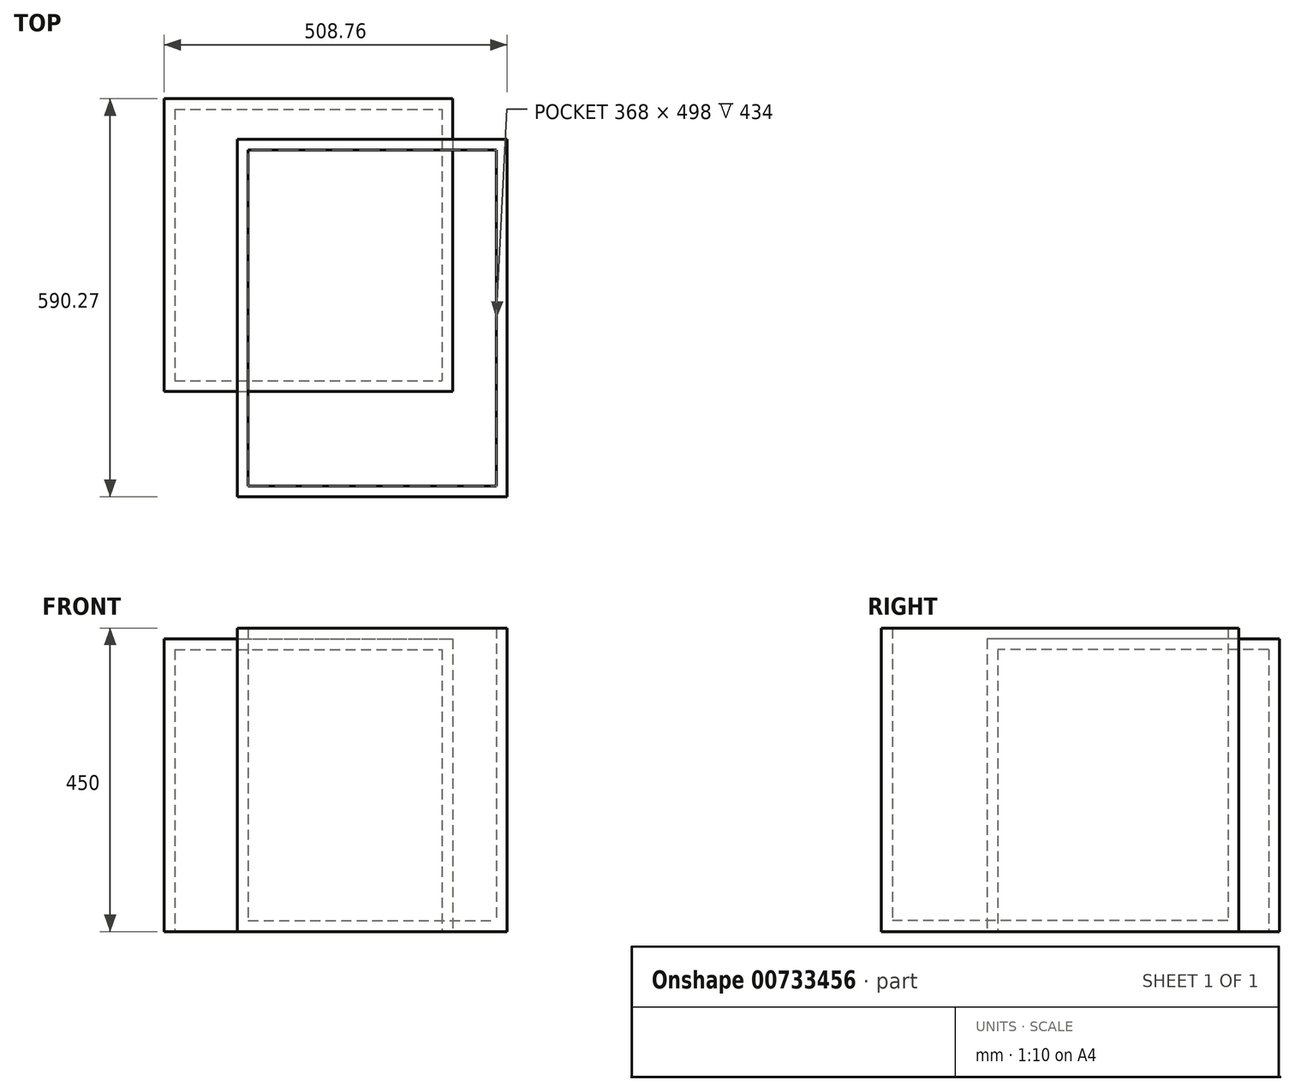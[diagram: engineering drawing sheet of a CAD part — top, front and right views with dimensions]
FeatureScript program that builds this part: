
annotation { "Feature Type Name" : "Feature", "Feature Type Description" : "" }
export const myFeature = defineFeature(function(context is Context, id is Id, definition is map)
    precondition{}
    {
        {
            var Q0;
            Q0=qCreatedBy(makeId("Top.planeOp"),FACE);
            var sketch = newSketch(context, id + "F0", { "sketchPlane" : qUnion([Q0])});
            skLineSegment(sketch, "E0.bottom", {"start": v(-203.64, 308.13) * mm, "end": v(196.36, 308.13) * mm});
            skLineSegment(sketch, "E0.top", {"start": v(-203.64, -221.87) * mm, "end": v(196.36, -221.87) * mm});
            skLineSegment(sketch, "E0.left", {"start": v(-203.64, 308.13) * mm, "end": v(-203.64, -221.87) * mm});
            skLineSegment(sketch, "E0.right", {"start": v(196.36, 308.13) * mm, "end": v(196.36, -221.87) * mm});
            skSolve(sketch);
        }
        {
            var Q0;
            Q0=makeQuery(id+"F0.imprint","IMPRINT",FACE,{"disambiguationData":[TD([[makeQuery(id+"F0.imprint","IMPRINT",EDGE,{"derivedFrom":sQuery(id+"F0.wireOp",EDGE,"E0.bottom")}),-1.0]])]});
            var sketch = newSketch(context, id + "F1", { "sketchPlane" : qUnion([Q0])});
            skLineSegment(sketch, "E1.bottom", {"start": v(-312.4, 368.4) * mm, "end": v(115.6, 368.4) * mm});
            skLineSegment(sketch, "E1.top", {"start": v(-312.4, -65.6) * mm, "end": v(115.6, -65.6) * mm});
            skLineSegment(sketch, "E1.left", {"start": v(-312.4, 368.4) * mm, "end": v(-312.4, -65.6) * mm});
            skLineSegment(sketch, "E1.right", {"start": v(115.6, 368.4) * mm, "end": v(115.6, -65.6) * mm});
            skSolve(sketch);
        }
        {
            var Q0;
            Q0 = qSketchRegion(id + "F0", true);
            extrude(context, id + "F2", {"entities" : qUnion([Q0]), "depth" : 450 * mm, "offsetDistance" : 25 * mm});
        }
        {
            var Q0;
            Q0=makeQuery(id+"F2.opExtrude","CAP_FACE",FACE,{"disambiguationData":[OSD([sQuery(id+"F0.wireOp",EDGE,"E0.bottom"),sQuery(id+"F0.wireOp",EDGE,"E0.top"),sQuery(id+"F0.wireOp",EDGE,"E0.left"),sQuery(id+"F0.wireOp",EDGE,"E0.right")])],"isStart":false});
            shell(context, id + "F3", {"entities" : qUnion([Q0]), "thickness" : 16 * mm});
        }
        {
            var Q0;
            Q0 = qSketchRegion(id + "F1", true);
            extrude(context, id + "F4", {"entities" : qUnion([Q0]), "depth" : 434 * mm, "offsetDistance" : 25 * mm});
        }
        {
            var Q0;
            Q0=makeQuery(id+"F4.opExtrude","CAP_FACE",FACE,{"disambiguationData":[OSD([sQuery(id+"F1.wireOp",EDGE,"E1.bottom"),sQuery(id+"F1.wireOp",EDGE,"E1.top"),sQuery(id+"F1.wireOp",EDGE,"E1.left"),sQuery(id+"F1.wireOp",EDGE,"E1.right")])],"isStart":true});
            shell(context, id + "F5", {"entities" : qUnion([Q0]), "thickness" : 16 * mm});
        }
    });
